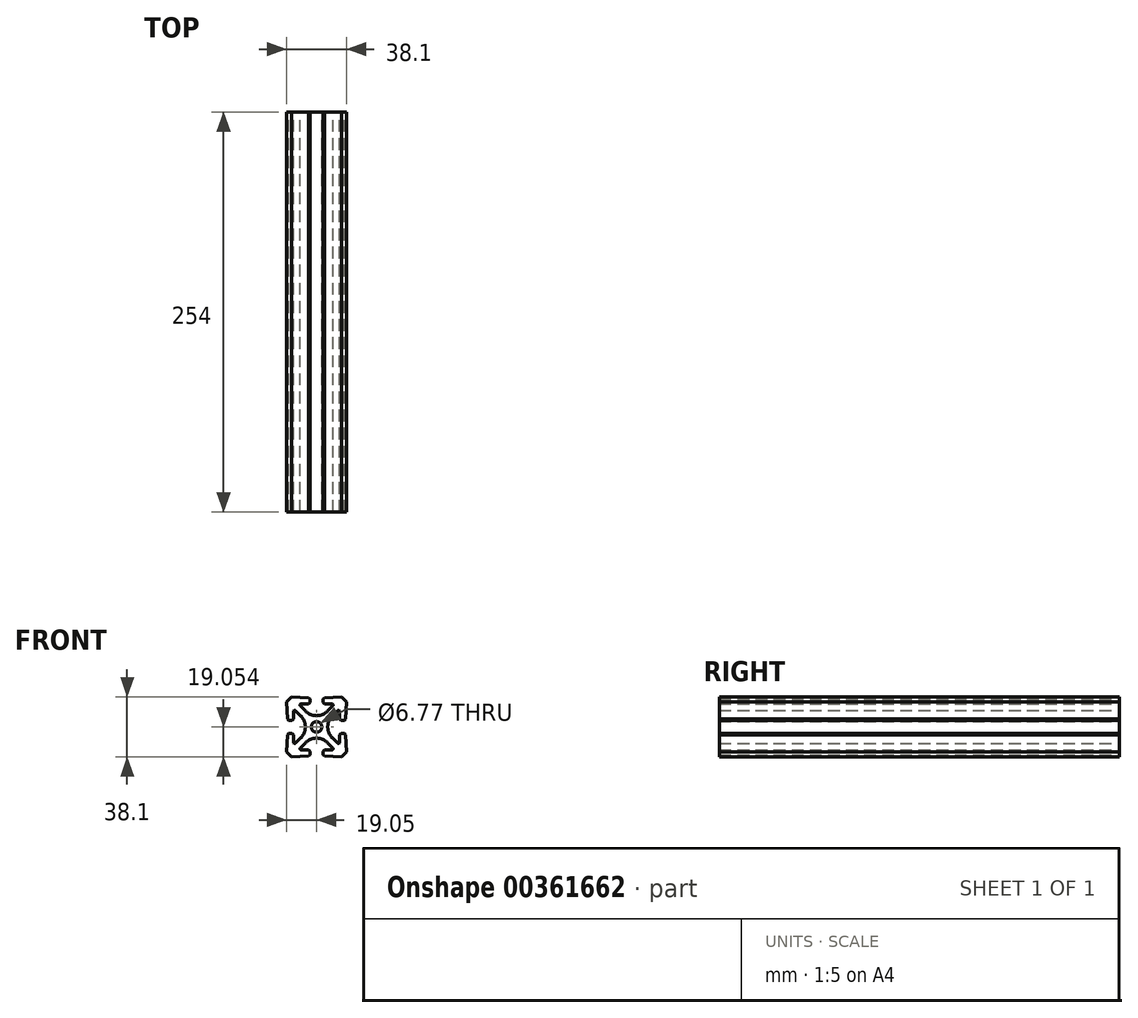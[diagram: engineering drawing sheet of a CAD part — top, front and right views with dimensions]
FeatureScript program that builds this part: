
annotation { "Feature Type Name" : "Feature", "Feature Type Description" : "" }
export const myFeature = defineFeature(function(context is Context, id is Id, definition is map)
    precondition{}
    {
        {
            var Q0;
            Q0=qCreatedBy(makeId("Front.planeOp"),FACE);
            var sketch = newSketch(context, id + "F0", { "sketchPlane" : qUnion([Q0])});
            skArc(sketch, "E0", {"start": v(-66.72, 24.5) * mm, "mid": v(-70.11, 27.88) * mm, "end": v(-73.5, 24.5) * mm});
            skArc(sketch, "E1", {"start": v(-73.5, 24.5) * mm, "mid": v(-70.11, 21.1) * mm, "end": v(-66.72, 24.5) * mm});
            skLineSegment(sketch, "E2", {"start": v(-54.24, 43.54) * mm, "end": v(-65.16, 42.97) * mm});
            skLineSegment(sketch, "E3", {"start": v(-65.16, 42.97) * mm, "end": v(-65.94, 42.14) * mm});
            skLineSegment(sketch, "E4", {"start": v(-65.94, 42.14) * mm, "end": v(-65.94, 39.96) * mm});
            skLineSegment(sketch, "E5", {"start": v(-65.94, 39.96) * mm, "end": v(-65.16, 39.18) * mm});
            skLineSegment(sketch, "E6", {"start": v(-65.16, 39.18) * mm, "end": v(-60.35, 39.18) * mm});
            skArc(sketch, "E7", {"start": v(-60.35, 39.18) * mm, "mid": v(-59.65, 38.7) * mm, "end": v(-59.81, 37.87) * mm});
            skLineSegment(sketch, "E8", {"start": v(-59.81, 37.87) * mm, "end": v(-63.19, 34.5) * mm});
            skArc(sketch, "E9", {"start": v(-63.19, 34.5) * mm, "mid": v(-66.36, 32.37) * mm, "end": v(-70.11, 31.63) * mm});
            skArc(sketch, "E10", {"start": v(-70.11, 31.63) * mm, "mid": v(-73.86, 32.37) * mm, "end": v(-77.03, 34.5) * mm});
            skLineSegment(sketch, "E11", {"start": v(-77.03, 34.5) * mm, "end": v(-80.4, 37.87) * mm});
            skArc(sketch, "E12", {"start": v(-80.4, 37.87) * mm, "mid": v(-80.57, 38.7) * mm, "end": v(-79.87, 39.18) * mm});
            skLineSegment(sketch, "E13", {"start": v(-79.87, 39.18) * mm, "end": v(-75.06, 39.18) * mm});
            skLineSegment(sketch, "E14", {"start": v(-75.06, 39.18) * mm, "end": v(-74.28, 39.96) * mm});
            skLineSegment(sketch, "E15", {"start": v(-74.28, 39.96) * mm, "end": v(-74.28, 42.14) * mm});
            skLineSegment(sketch, "E16", {"start": v(-74.28, 42.14) * mm, "end": v(-75.06, 42.97) * mm});
            skLineSegment(sketch, "E17", {"start": v(-75.06, 42.97) * mm, "end": v(-85.99, 43.54) * mm});
            skLineSegment(sketch, "E18", {"start": v(-85.99, 43.54) * mm, "end": v(-89.16, 40.37) * mm});
            skLineSegment(sketch, "E19", {"start": v(-89.16, 40.37) * mm, "end": v(-88.59, 29.45) * mm});
            skLineSegment(sketch, "E20", {"start": v(-88.59, 29.45) * mm, "end": v(-87.76, 28.66) * mm});
            skLineSegment(sketch, "E21", {"start": v(-87.76, 28.66) * mm, "end": v(-85.58, 28.66) * mm});
            skLineSegment(sketch, "E22", {"start": v(-85.58, 28.66) * mm, "end": v(-84.8, 29.45) * mm});
            skLineSegment(sketch, "E23", {"start": v(-84.8, 29.45) * mm, "end": v(-84.8, 34.25) * mm});
            skArc(sketch, "E24", {"start": v(-84.8, 34.25) * mm, "mid": v(-84.32, 34.96) * mm, "end": v(-83.5, 34.8) * mm});
            skLineSegment(sketch, "E25", {"start": v(-83.5, 34.8) * mm, "end": v(-80.12, 31.42) * mm});
            skArc(sketch, "E26", {"start": v(-80.12, 31.42) * mm, "mid": v(-77.99, 28.24) * mm, "end": v(-77.24, 24.5) * mm});
            skArc(sketch, "E27", {"start": v(-77.24, 24.5) * mm, "mid": v(-77.99, 20.75) * mm, "end": v(-80.12, 17.57) * mm});
            skLineSegment(sketch, "E28", {"start": v(-80.12, 17.57) * mm, "end": v(-83.5, 14.2) * mm});
            skArc(sketch, "E29", {"start": v(-83.5, 14.2) * mm, "mid": v(-84.32, 14.03) * mm, "end": v(-84.8, 14.74) * mm});
            skLineSegment(sketch, "E30", {"start": v(-84.8, 14.74) * mm, "end": v(-84.8, 19.54) * mm});
            skLineSegment(sketch, "E31", {"start": v(-84.8, 19.54) * mm, "end": v(-85.58, 20.33) * mm});
            skLineSegment(sketch, "E32", {"start": v(-85.58, 20.33) * mm, "end": v(-87.76, 20.33) * mm});
            skLineSegment(sketch, "E33", {"start": v(-87.76, 20.33) * mm, "end": v(-88.59, 19.54) * mm});
            skLineSegment(sketch, "E34", {"start": v(-88.59, 19.54) * mm, "end": v(-89.16, 8.62) * mm});
            skLineSegment(sketch, "E35", {"start": v(-89.16, 8.62) * mm, "end": v(-85.99, 5.44) * mm});
            skLineSegment(sketch, "E36", {"start": v(-85.99, 5.44) * mm, "end": v(-75.06, 6.02) * mm});
            skLineSegment(sketch, "E37", {"start": v(-75.06, 6.02) * mm, "end": v(-74.28, 6.85) * mm});
            skLineSegment(sketch, "E38", {"start": v(-74.28, 6.85) * mm, "end": v(-74.28, 9.03) * mm});
            skLineSegment(sketch, "E39", {"start": v(-74.28, 9.03) * mm, "end": v(-75.06, 9.81) * mm});
            skLineSegment(sketch, "E40", {"start": v(-75.06, 9.81) * mm, "end": v(-79.87, 9.81) * mm});
            skArc(sketch, "E41", {"start": v(-79.87, 9.81) * mm, "mid": v(-80.57, 10.28) * mm, "end": v(-80.4, 11.11) * mm});
            skLineSegment(sketch, "E42", {"start": v(-80.4, 11.11) * mm, "end": v(-77.03, 14.49) * mm});
            skArc(sketch, "E43", {"start": v(-77.03, 14.49) * mm, "mid": v(-73.86, 16.61) * mm, "end": v(-70.11, 17.36) * mm});
            skArc(sketch, "E44", {"start": v(-70.11, 17.36) * mm, "mid": v(-66.36, 16.61) * mm, "end": v(-63.19, 14.49) * mm});
            skLineSegment(sketch, "E45", {"start": v(-63.19, 14.49) * mm, "end": v(-59.81, 11.11) * mm});
            skArc(sketch, "E46", {"start": v(-59.81, 11.11) * mm, "mid": v(-59.65, 10.28) * mm, "end": v(-60.35, 9.81) * mm});
            skLineSegment(sketch, "E47", {"start": v(-60.35, 9.81) * mm, "end": v(-65.16, 9.81) * mm});
            skLineSegment(sketch, "E48", {"start": v(-65.16, 9.81) * mm, "end": v(-65.94, 9.03) * mm});
            skLineSegment(sketch, "E49", {"start": v(-65.94, 9.03) * mm, "end": v(-65.94, 6.85) * mm});
            skLineSegment(sketch, "E50", {"start": v(-65.94, 6.85) * mm, "end": v(-65.16, 6.02) * mm});
            skLineSegment(sketch, "E51", {"start": v(-65.16, 6.02) * mm, "end": v(-54.24, 5.44) * mm});
            skLineSegment(sketch, "E52", {"start": v(-54.24, 5.44) * mm, "end": v(-51.06, 8.62) * mm});
            skLineSegment(sketch, "E53", {"start": v(-51.06, 8.62) * mm, "end": v(-51.63, 19.54) * mm});
            skLineSegment(sketch, "E54", {"start": v(-51.63, 19.54) * mm, "end": v(-52.46, 20.33) * mm});
            skLineSegment(sketch, "E55", {"start": v(-52.46, 20.33) * mm, "end": v(-54.64, 20.33) * mm});
            skLineSegment(sketch, "E56", {"start": v(-54.64, 20.33) * mm, "end": v(-55.43, 19.54) * mm});
            skLineSegment(sketch, "E57", {"start": v(-55.43, 19.54) * mm, "end": v(-55.43, 14.74) * mm});
            skArc(sketch, "E58", {"start": v(-55.43, 14.74) * mm, "mid": v(-55.9, 14.03) * mm, "end": v(-56.73, 14.2) * mm});
            skLineSegment(sketch, "E59", {"start": v(-56.73, 14.2) * mm, "end": v(-60.1, 17.57) * mm});
            skArc(sketch, "E60", {"start": v(-60.1, 17.57) * mm, "mid": v(-62.23, 20.75) * mm, "end": v(-62.98, 24.5) * mm});
            skArc(sketch, "E61", {"start": v(-62.98, 24.5) * mm, "mid": v(-62.23, 28.24) * mm, "end": v(-60.1, 31.42) * mm});
            skLineSegment(sketch, "E62", {"start": v(-60.1, 31.42) * mm, "end": v(-56.73, 34.8) * mm});
            skArc(sketch, "E63", {"start": v(-56.73, 34.8) * mm, "mid": v(-55.9, 34.96) * mm, "end": v(-55.43, 34.25) * mm});
            skLineSegment(sketch, "E64", {"start": v(-55.43, 34.25) * mm, "end": v(-55.43, 29.45) * mm});
            skLineSegment(sketch, "E65", {"start": v(-55.43, 29.45) * mm, "end": v(-54.64, 28.66) * mm});
            skLineSegment(sketch, "E66", {"start": v(-54.64, 28.66) * mm, "end": v(-52.46, 28.66) * mm});
            skLineSegment(sketch, "E67", {"start": v(-52.46, 28.66) * mm, "end": v(-51.63, 29.45) * mm});
            skLineSegment(sketch, "E68", {"start": v(-51.63, 29.45) * mm, "end": v(-51.06, 40.37) * mm});
            skLineSegment(sketch, "E69", {"start": v(-51.06, 40.37) * mm, "end": v(-54.24, 43.54) * mm});
            skSolve(sketch);
        }
        {
            var Q0;
            Q0 = qSketchRegion(id + "F0", true);
            extrude(context, id + "F1", {"entities" : qUnion([Q0]), "depth" : 254 * mm});
        }
    });
